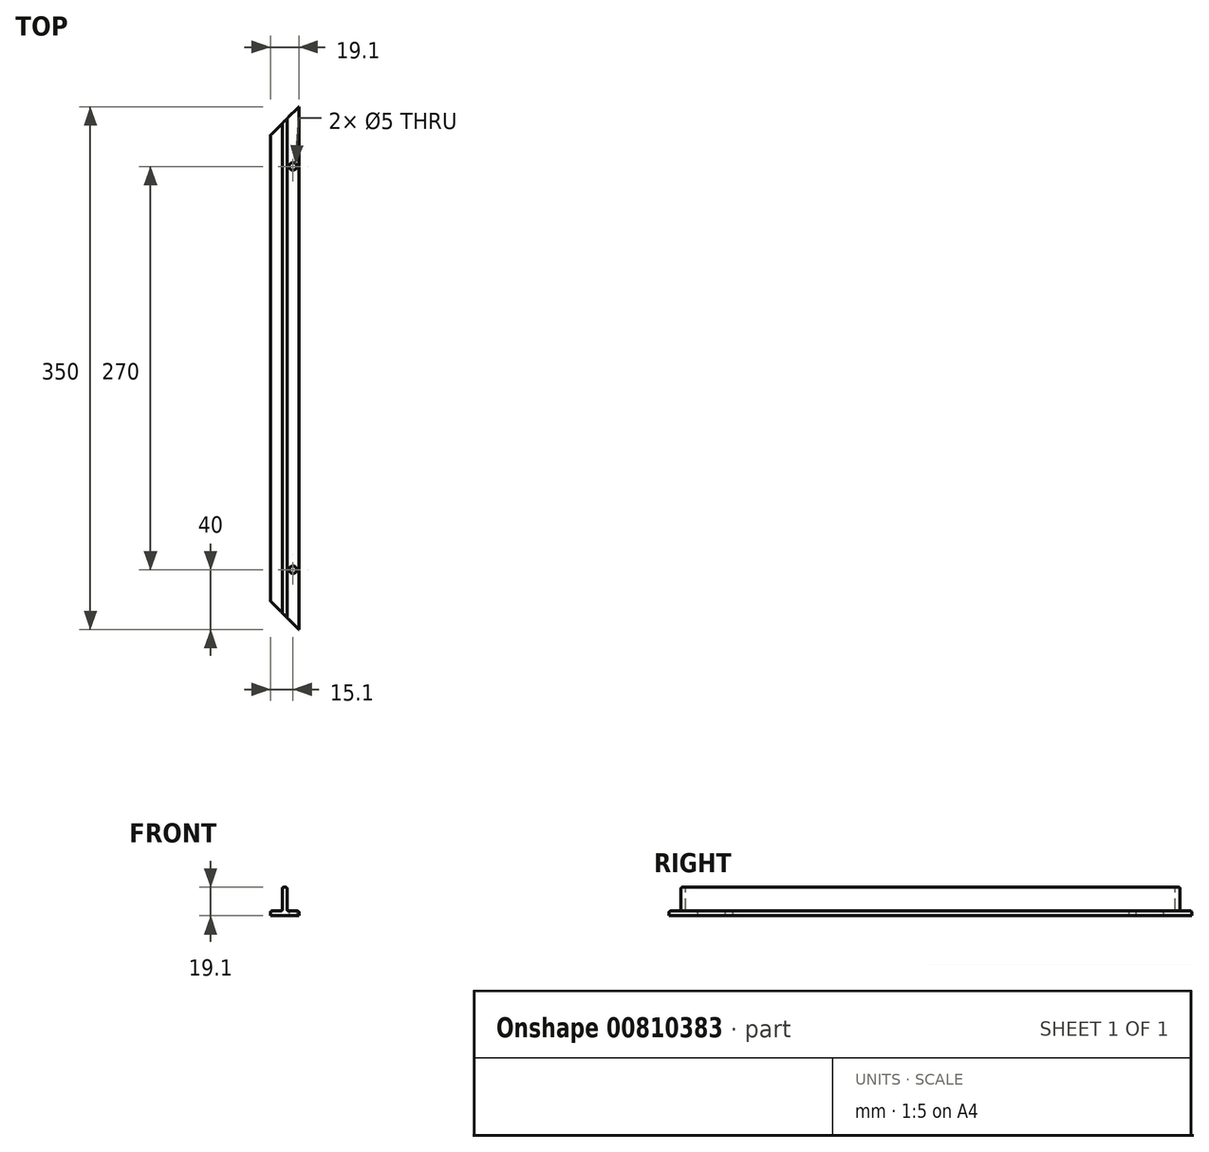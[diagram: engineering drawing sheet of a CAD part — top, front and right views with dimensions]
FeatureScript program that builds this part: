
annotation { "Feature Type Name" : "Feature", "Feature Type Description" : "" }
export const myFeature = defineFeature(function(context is Context, id is Id, definition is map)
    precondition{}
    {
        {
            var Q0;
            Q0=qCreatedBy(makeId("Front.planeOp"),FACE);
            var sketch = newSketch(context, id + "F0", { "sketchPlane" : qUnion([Q0])});
            skLineSegment(sketch, "E0", {"start": v(-9.55, 0) * mm, "end": v(9.55, 0) * mm});
            skLineSegment(sketch, "E1", {"start": v(9.55, 0) * mm, "end": v(9.55, 2.17) * mm});
            skLineSegment(sketch, "E2", {"start": v(8.55, 3.17) * mm, "end": v(2.58, 3.17) * mm});
            skLineSegment(sketch, "E3", {"start": v(1.58, 4.17) * mm, "end": v(1.58, 18.1) * mm});
            skLineSegment(sketch, "E4", {"start": v(0.58, 19.1) * mm, "end": v(-0.59, 19.1) * mm});
            skLineSegment(sketch, "E5", {"start": v(-1.59, 18.1) * mm, "end": v(-1.59, 4.17) * mm});
            skLineSegment(sketch, "E6", {"start": v(-2.59, 3.17) * mm, "end": v(-8.55, 3.17) * mm});
            skLineSegment(sketch, "E7", {"start": v(-9.55, 2.17) * mm, "end": v(-9.55, 0) * mm});
            skPoint(sketch, "E8.visualSharp", {"position": v(-9.55, 3.17) * mm});
            skArc(sketch, "E8.filletArc", {"start": v(-8.55, 3.17) * mm, "mid": v(-9.26, 2.88) * mm, "end": v(-9.55, 2.17) * mm});
            skPoint(sketch, "E9.visualSharp", {"position": v(9.55, 3.17) * mm});
            skArc(sketch, "E9.filletArc", {"start": v(9.55, 2.17) * mm, "mid": v(9.26, 2.88) * mm, "end": v(8.55, 3.17) * mm});
            skPoint(sketch, "E10.visualSharp", {"position": v(1.58, 19.1) * mm});
            skArc(sketch, "E10.filletArc", {"start": v(1.58, 18.1) * mm, "mid": v(1.3, 18.8) * mm, "end": v(0.58, 19.1) * mm});
            skPoint(sketch, "E11.visualSharp", {"position": v(-1.59, 19.1) * mm});
            skArc(sketch, "E11.filletArc", {"start": v(-0.59, 19.1) * mm, "mid": v(-1.3, 18.8) * mm, "end": v(-1.59, 18.1) * mm});
            skPoint(sketch, "E12.visualSharp", {"position": v(1.58, 3.17) * mm});
            skArc(sketch, "E12.filletArc", {"start": v(1.58, 4.17) * mm, "mid": v(1.88, 3.46) * mm, "end": v(2.58, 3.17) * mm});
            skPoint(sketch, "E13.visualSharp", {"position": v(-1.59, 3.17) * mm});
            skArc(sketch, "E13.filletArc", {"start": v(-2.59, 3.17) * mm, "mid": v(-1.88, 3.46) * mm, "end": v(-1.59, 4.17) * mm});
            skSolve(sketch);
        }
        {
            var Q0;
            Q0=makeQuery(id+"F0.imprint","IMPRINT",FACE,{"disambiguationData":[TD([[makeQuery(id+"F0.imprint","IMPRINT",EDGE,{"derivedFrom":sQuery(id+"F0.wireOp",EDGE,"E0")}),1.0]])]});
            extrude(context, id + "F1", {"entities" : qUnion([Q0]), "depth" : 350 * mm, "offsetDistance" : 25 * mm});
        }
        {
            var Q0;
            Q0=makeQuery(id+"F1.opExtrude","SWEPT_FACE",FACE,{"disambiguationData":[OSD([sQuery(id+"F0.wireOp",EDGE,"E0")])]});
            var sketch = newSketch(context, id + "F2", { "sketchPlane" : qUnion([Q0])});
            skLineSegment(sketch, "E14", {"start": v(9.55, 350) * mm, "end": v(-9.55, 350) * mm});
            skLineSegment(sketch, "E15", {"start": v(-9.55, 350) * mm, "end": v(-9.55, 330.9) * mm});
            skLineSegment(sketch, "E16", {"start": v(-9.55, 330.9) * mm, "end": v(9.55, 350) * mm});
            skLineSegment(sketch, "E17", {"start": v(9.55, 175) * mm, "end": v(-9.55, 175) * mm, "construction": true});
            skLineSegment(sketch, "E18.MirrorCS", {"start": v(-9.55, 19.1) * mm, "end": v(9.55, 0) * mm});
            skLineSegment(sketch, "E19.MirrorCS", {"start": v(9.55, 0) * mm, "end": v(-9.55, 0) * mm});
            skLineSegment(sketch, "E20.MirrorCS", {"start": v(-9.55, 0) * mm, "end": v(-9.55, 19.1) * mm});
            skSolve(sketch);
        }
        {
            var Q0;
            Q0=makeQuery(id+"F2.imprint","IMPRINT",FACE,{"disambiguationData":[TD([[makeQuery(id+"F2.imprint","IMPRINT",EDGE,{"derivedFrom":sQuery(id+"F2.wireOp",EDGE,"E14")}),-1.0]])]});
            var Q1;
            Q1=makeQuery(id+"F2.imprint","IMPRINT",FACE,{"disambiguationData":[TD([[makeQuery(id+"F2.imprint","IMPRINT",EDGE,{"derivedFrom":sQuery(id+"F2.wireOp",EDGE,"E18.MirrorCS")}),-1.0]])]});
            extrude(context, id + "F3", {"entities" : qUnion([Q0, Q1]), "operationType" : NewBodyOperationType.REMOVE, "oppositeDirection" : true, "depth" : 20 * mm, "offsetDistance" : 25 * mm});
        }
        {
            var Q0;
            Q0=makeQuery(id+"F1.opExtrude","SWEPT_FACE",FACE,{"disambiguationData":[OSD([sQuery(id+"F0.wireOp",EDGE,"E0")])]});
            var sketch = newSketch(context, id + "F4", { "sketchPlane" : qUnion([Q0])});
            skLineSegment(sketch, "E21", {"start": v(9.55, 350) * mm, "end": v(9.55, 310) * mm});
            skLineSegment(sketch, "E22", {"start": v(9.55, 310) * mm, "end": v(5.55, 310) * mm});
            skLineSegment(sketch, "E23", {"start": v(9.55, 0) * mm, "end": v(9.55, 40) * mm});
            skLineSegment(sketch, "E24", {"start": v(9.55, 40) * mm, "end": v(5.55, 40) * mm});
            skPoint(sketch, "E25", {"position": v(5.55, 310) * mm});
            skPoint(sketch, "E26", {"position": v(5.55, 40) * mm});
            skSolve(sketch);
        }
        {
            var Q0;
            Q0=sQuery(id+"F4.wireOp",VERTEX,"E25");
            var Q1;
            Q1=sQuery(id+"F4.wireOp",VERTEX,"E26");
            var Q2;
            Q2=makeQuery(id+"F1.opExtrude","SWEPT_BODY",BODY,{"disambiguationData":[OSD([sQuery(id+"F0.wireOp",EDGE,"E0"),sQuery(id+"F0.wireOp",EDGE,"E1"),sQuery(id+"F0.wireOp",EDGE,"E2"),sQuery(id+"F0.wireOp",EDGE,"E3"),sQuery(id+"F0.wireOp",EDGE,"E4"),sQuery(id+"F0.wireOp",EDGE,"E5"),sQuery(id+"F0.wireOp",EDGE,"E6"),sQuery(id+"F0.wireOp",EDGE,"E7"),sQuery(id+"F0.wireOp",EDGE,"E8.filletArc"),sQuery(id+"F0.wireOp",EDGE,"E9.filletArc"),sQuery(id+"F0.wireOp",EDGE,"E10.filletArc"),sQuery(id+"F0.wireOp",EDGE,"E11.filletArc"),sQuery(id+"F0.wireOp",EDGE,"E12.filletArc"),sQuery(id+"F0.wireOp",EDGE,"E13.filletArc")])]});
            hole(context, id + "F5", {"style" : HoleStyle.SIMPLE, "endStyle" : HoleEndStyle.THROUGH, "holeDiameter" : 5 * mm, "majorDiameter" : 5 * mm, "isTappedThrough" : true, "tappedDepth" : 12 * mm, "tapClearance" : 3, "locations" : qUnion([Q0, Q1]), "scope" : qUnion([Q2])});
        }
    });
